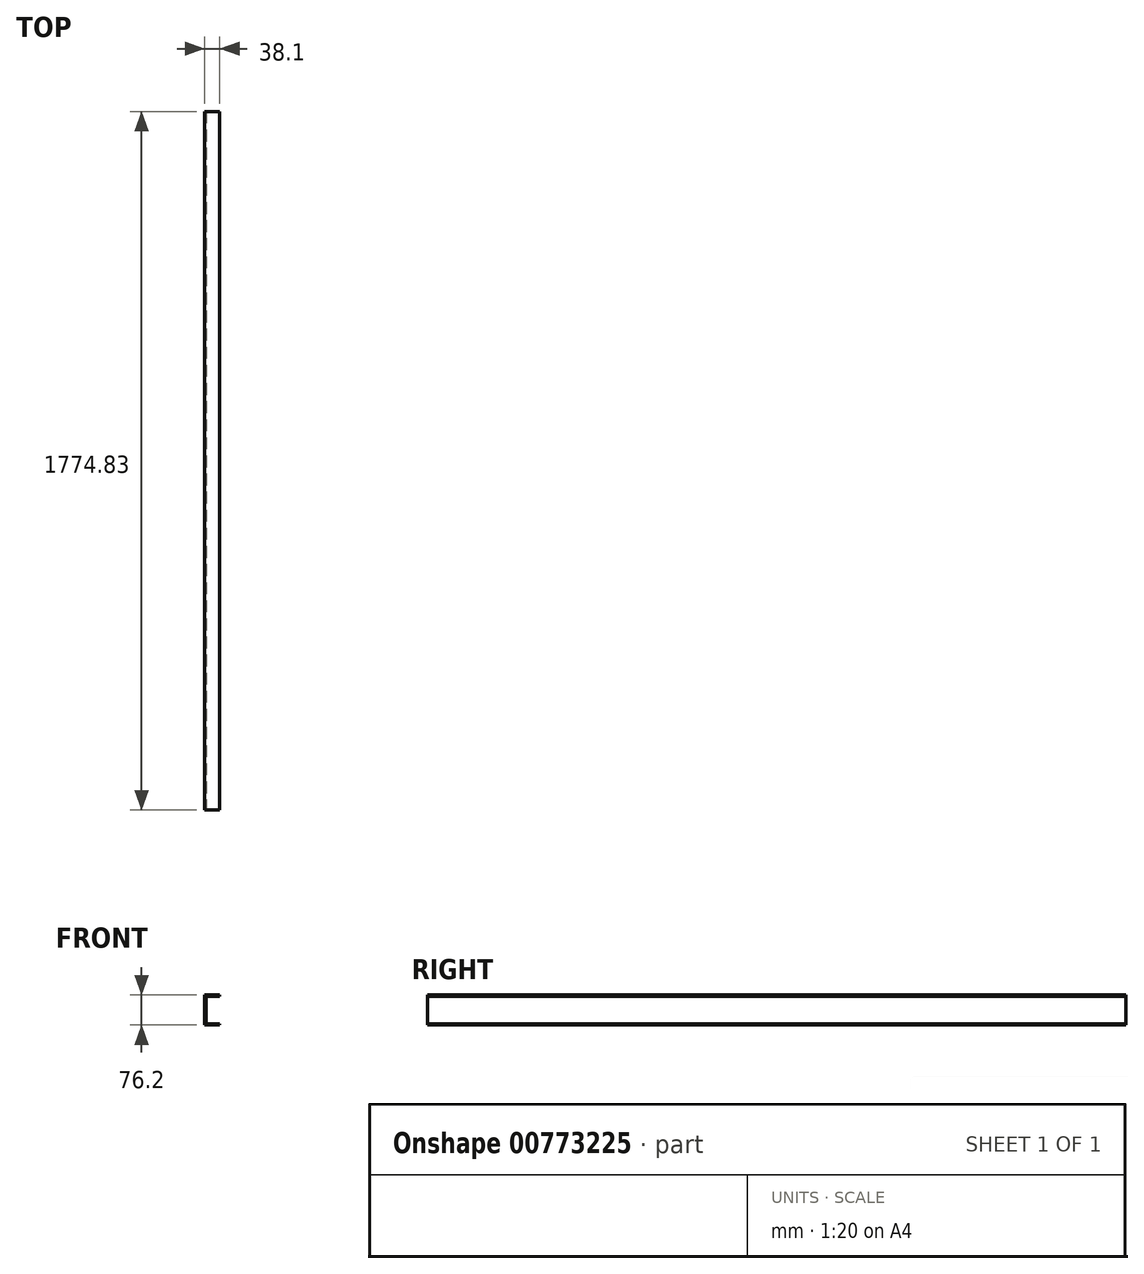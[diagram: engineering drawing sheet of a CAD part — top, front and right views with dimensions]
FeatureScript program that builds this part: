
annotation { "Feature Type Name" : "Feature", "Feature Type Description" : "" }
export const myFeature = defineFeature(function(context is Context, id is Id, definition is map)
    precondition{}
    {
        {
            var Q0;
            Q0=qCreatedBy(makeId("Front.planeOp"),FACE);
            var sketch = newSketch(context, id + "F0", { "sketchPlane" : qUnion([Q0])});
            skLineSegment(sketch, "E0", {"start": v(0, 0) * mm, "end": v(0, 76.2) * mm});
            skLineSegment(sketch, "E1", {"start": v(0, 76.2) * mm, "end": v(38.1, 76.2) * mm});
            skLineSegment(sketch, "E2", {"start": v(38.1, 76.2) * mm, "end": v(38.1, 73.03) * mm});
            skLineSegment(sketch, "E3", {"start": v(38.1, 73.03) * mm, "end": v(3.17, 73.03) * mm});
            skLineSegment(sketch, "E4", {"start": v(3.17, 73.03) * mm, "end": v(3.18, 3.17) * mm});
            skLineSegment(sketch, "E5", {"start": v(3.18, 3.17) * mm, "end": v(38.1, 3.17) * mm});
            skLineSegment(sketch, "E6", {"start": v(38.1, 3.18) * mm, "end": v(38.1, 0) * mm});
            skLineSegment(sketch, "E7", {"start": v(38.1, 0) * mm, "end": v(0, 0) * mm});
            skSolve(sketch);
        }
        {
            var Q0;
            Q0=qSketchRegion(id+"F0",true);
            extrude(context, id + "F1", {"entities" : qUnion([Q0]), "oppositeDirection" : true, "depth" : 1774.82 * mm, "offsetDistance" : 25.4 * mm});
        }
    });
